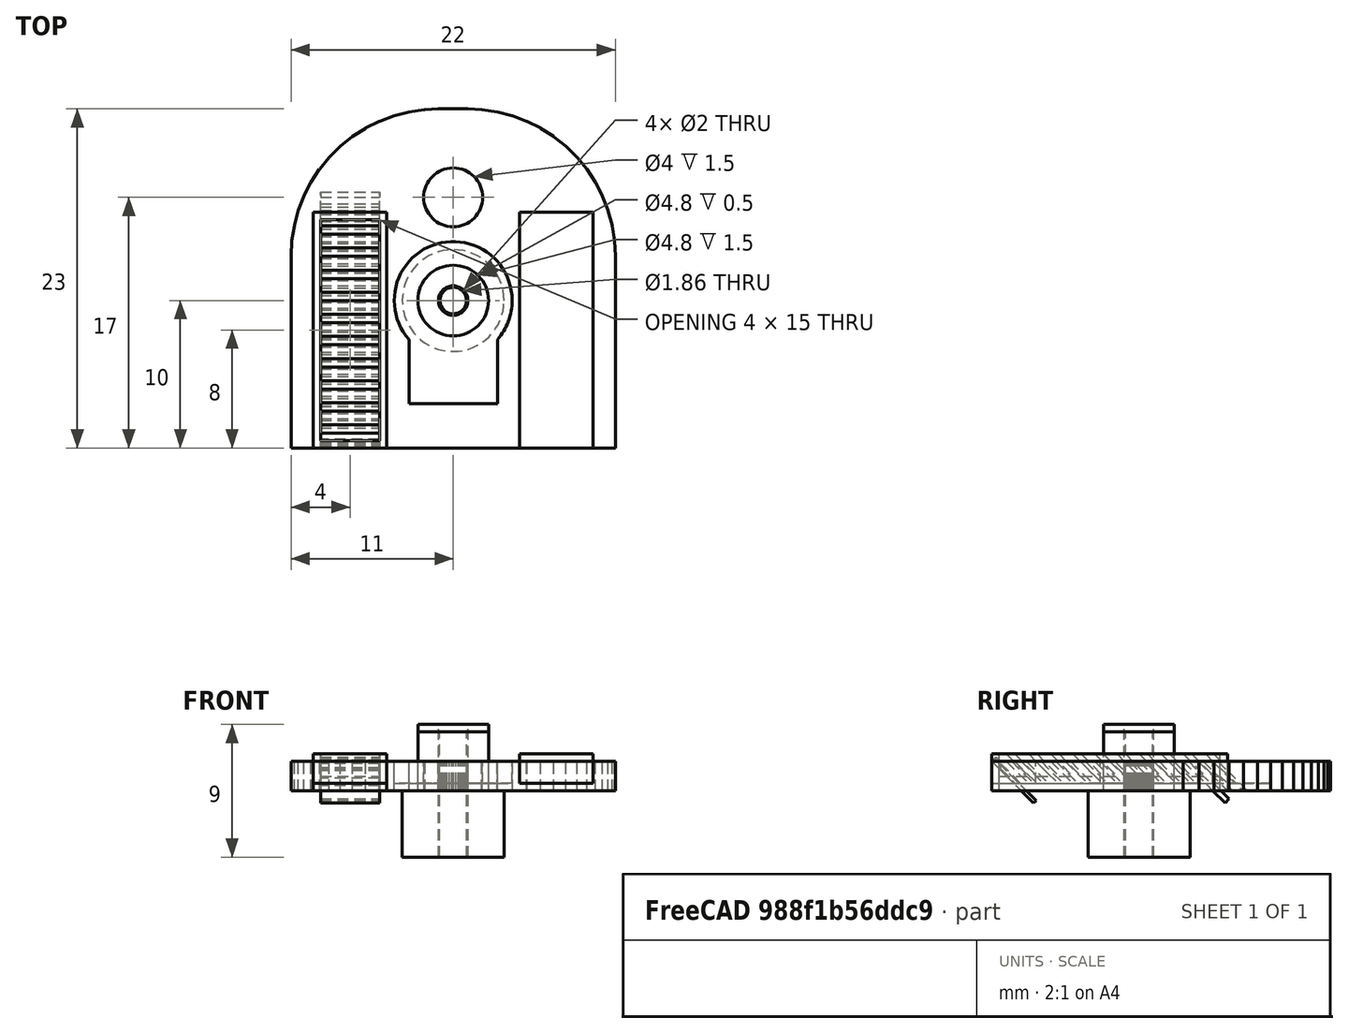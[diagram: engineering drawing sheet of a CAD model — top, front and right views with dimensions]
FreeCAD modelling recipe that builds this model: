
FCSTD DOCUMENT  (FreeCAD 0.18.3R)
Label: Engine Cowling
License: All rights reserved
LicenseURL: http://en.wikipedia.org/wiki/All_rights_reserved
objects: Part::Feature×39, Part::FeaturePython×34, Part::Box×11, Part::Cylinder×8, App::DocumentObjectGroup×8, Part::Cut×6, Part::MultiFuse×2, Mesh::Feature×1, Part::Extrusion×1
note: 101 computed .brp shape members not serialized (recipe doc carries the construction recipe); baked Part::Feature solids carry a one-line shape summary decoded from their .brp

FEATURE [Part::Cylinder] Cylinder003010  label="Cowling Insert Round002"
  Angle = 360
  AttacherType = Attacher::AttachEngine3D
  Height = 1.5
  Placement = pos=(11,17,0.5) rot=(0,0,1;0rad)
  Radius = 2
FEATURE [Part::Box] Box001005010013  label="Cube051"
  AttacherType = Attacher::AttachEngine3D
  Height = 1.5
  Length = 6
  Placement = pos=(8,3,0.5) rot=(0,0,1;0rad)
  Width = 7
FEATURE [Part::Cylinder] Cylinder003011  label="Cylinder012"
  Angle = 360
  AttacherType = Attacher::AttachEngine3D
  Height = 1.5
  Placement = pos=(11,10,0.5) rot=(0,0,1;0rad)
  Radius = 4
FEATURE [Part::MultiFuse] Fusion  label="Cowling Insert Keyhole Old"
  Shapes = -> [Box001005010013,Cylinder003011]
FEATURE [Mesh::Feature] Engine_Cowling  label="Engine Cowling"
FEATURE [Part::Feature] Engine_Cowling001
  Placement = pos=(0,0,-0.51311) rot=(0,0,1;0rad)
  shape: bbox 22 x 23 x 2.5 mm, 1292 faces, 0 solids (baked)
FEATURE [Part::Cylinder] Cylinder003006  label="Cylinder007"
  Angle = 360
  AttacherType = Attacher::AttachEngine3D
  Height = 20
  Placement = pos=(11,10,-8) rot=(0,0,1;0rad)
  Radius = 1
FEATURE [Part::Cylinder] Cylinder003005  label="Cylinder006"
  Angle = 360
  AttacherType = Attacher::AttachEngine3D
  Height = 4.5
  Placement = pos=(11,10,-5) rot=(0,0,1;0rad)
  Radius = 3.45
FEATURE [Part::Cut] Cut002002002012
  Base = -> Cylinder003005
  Tool = -> Cylinder003006
FEATURE [Part::Cylinder] Cylinder003003  label="Cylinder004"
  Angle = 360
  AttacherType = Attacher::AttachEngine3D
  Height = 4.5
  Placement = pos=(11,10,-0.5) rot=(0.707107,0,0.707107;0rad)
  Radius = 2.4
FEATURE [Part::Cut] Cut002002002013
  Base = -> Cylinder003003
  Tool = -> Cylinder003006
FEATURE [Part::FeaturePython] Connect006  label="Propeller Hub Old"  # WARN: FeaturePython — macro-defined, semantics opaque (R4)
  Objects = -> [Cut002002002012,Cut002002002013]
  Placement = pos=(0,0,0.5) rot=(0,0,1;0rad)
  Tolerance = 0
FEATURE [Part::Feature] Engine_Cowling001_cs
  Placement = pos=(0,0,-0.01) rot=(0,0,1;0rad)
  shape: bbox 22 x 23 x 3e-07 mm, 0 faces, 0 solids (baked)
FEATURE [Part::Extrusion] Extrude
  Base = -> Engine_Cowling001_cs
  Dir = (0,0,1)
  DirMode = 0
  FaceMakerClass = Part::FaceMakerBullseye
  LengthFwd = 2
  LengthRev = 0
  Solid = true
  Symmetric = false
FEATURE [Part::Box] Box  label="Cube"
  AttacherType = Attacher::AttachEngine3D
  Height = 2
  Length = 5
  Placement = pos=(1.5,0,0) rot=(0,0,1;0rad)
  Width = 16
FEATURE [Part::Box] Box001005010014  label="Cube052"
  AttacherType = Attacher::AttachEngine3D
  Height = 2
  Length = 4
  Placement = pos=(2,0.5,0.5) rot=(0,0,1;0rad)
  Width = 15
FEATURE [Part::Box] Box001005010015  label="Cube053"
  AttacherType = Attacher::AttachEngine3D
  Height = 0.25
  Length = 4
  Placement = pos=(2,0,2) rot=(-1,0,0;0.785398rad)
  Width = 4
FEATURE [Part::Cut] Cut
  Base = -> Box
  Tool = -> Box001005010014
FEATURE [Part::Feature] Face004
  Placement = pos=(1.5,0,0) rot=(0,0,1;0rad)
  shape: bbox 5 x 16 x 2e-07 mm, 1 faces, 0 solids (baked)
FEATURE [Part::Feature] Face005
  Placement = pos=(1.5,0,0) rot=(0,0,1;0rad)
  shape: bbox 5 x 16 x 2e-07 mm, 1 faces, 0 solids (baked)
FEATURE [Part::FeaturePython] Slice  # WARN: FeaturePython — macro-defined, semantics opaque (R4)
  Base = -> Box001005010015
  Mode = 1
  Tolerance = 0
  Tools = -> [Face004,Face005]
FEATURE [Part::FeaturePython] Slice_child0  label="Slice.0"  # WARN: FeaturePython — macro-defined, semantics opaque (R4)
  Base = -> Slice
  FilterType = 1
  Invert = false
  OverrideMaxVal = 0
  WindowFrom = 80
  WindowTo = 100
  items = 0
FEATURE [Part::FeaturePython] Slice_child1  label="Slice.1"  # WARN: FeaturePython — macro-defined, semantics opaque (R4)
  Base = -> Slice
  FilterType = 1
  Invert = false
  OverrideMaxVal = 0
  WindowFrom = 80
  WindowTo = 100
  items = 1
FEATURE [Part::FeaturePython] Slice_child2  label="Slice.2"  # WARN: FeaturePython — macro-defined, semantics opaque (R4)
  Base = -> Slice
  FilterType = 1
  Invert = false
  OverrideMaxVal = 0
  WindowFrom = 80
  WindowTo = 100
  items = 2
FEATURE [App::DocumentObjectGroup] GrExplode_Slice  label="Exploded Slice"
  Group = -> [Slice_child0,Slice_child1,Slice_child2]
FEATURE [Part::Feature] Slice_child0001  label="Slice.003"
  shape: bbox 4 x 2.354 x 2 mm, 6 faces (baked)
FEATURE [Part::Feature] Slice_child0002  label="Slice.004"
  Placement = pos=(0,1,0) rot=(0,0,1;0rad)
  shape: bbox 4 x 2.354 x 2 mm, 6 faces (baked)
FEATURE [Part::Feature] Slice_child0015  label="Slice.017"
  Placement = pos=(0,14,0) rot=(0,0,1;0rad)
  shape: bbox 4 x 2.354 x 2 mm, 6 faces (baked)
FEATURE [Part::Feature] Slice_child0016  label="Slice.018"
  Placement = pos=(0,15,0) rot=(0,0,1;0rad)
  shape: bbox 4 x 2.354 x 2 mm, 6 faces (baked)
FEATURE [Part::Box] Box001005010016  label="Cube054"
  AttacherType = Attacher::AttachEngine3D
  Height = 2
  Length = 5
  Placement = pos=(1.5,0,0) rot=(0,0,1;0rad)
  Width = 16
FEATURE [Part::FeaturePython] Slice001  # WARN: FeaturePython — macro-defined, semantics opaque (R4)
  Base = -> Slice_child0016
  Mode = 1
  Tolerance = 0
  Tools = -> [Box001005010016]
FEATURE [Part::FeaturePython] Slice001_child0  label="Slice001.0"  # WARN: FeaturePython — macro-defined, semantics opaque (R4)
  Base = -> Slice001
  FilterType = 1
  Invert = false
  OverrideMaxVal = 0
  WindowFrom = 80
  WindowTo = 100
  items = 0
FEATURE [Part::FeaturePython] Slice001_child1  label="Slice001.1"  # WARN: FeaturePython — macro-defined, semantics opaque (R4)
  Base = -> Slice001
  FilterType = 1
  Invert = false
  OverrideMaxVal = 0
  WindowFrom = 80
  WindowTo = 100
  items = 1
FEATURE [App::DocumentObjectGroup] GrExplode_Slice001  label="Exploded Slice001"
  Group = -> [Slice001_child0,Slice001_child1]
FEATURE [Part::Feature] Face008
  Placement = pos=(1.5,0,0) rot=(0,0,1;0rad)
  shape: bbox 5 x 2e-07 x 2 mm, 1 faces, 0 solids (baked)
FEATURE [Part::FeaturePython] Slice002  # WARN: FeaturePython — macro-defined, semantics opaque (R4)
  Base = -> Slice_child0015
  Mode = 1
  Tolerance = 0
  Tools = -> [Face008]
FEATURE [Part::FeaturePython] Slice002_child0  label="Slice002.0"  # WARN: FeaturePython — macro-defined, semantics opaque (R4)
  Base = -> Slice002
  FilterType = 1
  Invert = false
  OverrideMaxVal = 0
  WindowFrom = 80
  WindowTo = 100
  items = 0
FEATURE [Part::FeaturePython] Slice002_child1  label="Slice002.1"  # WARN: FeaturePython — macro-defined, semantics opaque (R4)
  Base = -> Slice002
  FilterType = 1
  Invert = false
  OverrideMaxVal = 0
  WindowFrom = 80
  WindowTo = 100
  items = 1
FEATURE [App::DocumentObjectGroup] GrExplode_Slice002  label="Exploded Slice002"
  Group = -> [Slice002_child0,Slice002_child1]
FEATURE [Part::Feature] Cut002002002014
  shape: bbox 5 x 16 x 2 mm, 11 faces (baked)
FEATURE [Part::Cut] Cut002002002015
  Base = -> Slice_child0001
  Tool = -> Cut002002002014
FEATURE [Part::Feature] Slice_child0017  label="Slice.019"
  shape: bbox 4 x 2.354 x 2 mm, 6 faces (baked)
FEATURE [Part::Feature] Cut002002002016
  shape: bbox 5 x 16 x 2 mm, 11 faces (baked)
FEATURE [Part::Cut] Cut002002002017
  Base = -> Slice_child0017
  Placement = pos=(0,0.1,0) rot=(0,0,1;0rad)
  Tool = -> Cut002002002016
FEATURE [Part::Feature] Slice_child0006  label="Slice.008"
  Placement = pos=(0,5,0) rot=(0,0,1;0rad)
  shape: bbox 4 x 2.354 x 2 mm, 6 faces (baked)
FEATURE [Part::Feature] Slice_child0004  label="Slice.006"
  Placement = pos=(0,3,0) rot=(0,0,1;0rad)
  shape: bbox 4 x 2.354 x 2 mm, 6 faces (baked)
FEATURE [Part::Feature] Slice_child0005  label="Slice.007"
  Placement = pos=(0,4,0) rot=(0,0,1;0rad)
  shape: bbox 4 x 2.354 x 2 mm, 6 faces (baked)
FEATURE [Part::Feature] Slice001_child0001  label="Slice001.002"
  shape: bbox 4 x 1 x 1 mm, 6 faces (baked)
FEATURE [Part::Feature] Slice002_child0001  label="Slice002.002"
  shape: bbox 4 x 2 x 2 mm, 6 faces (baked)
FEATURE [Part::Feature] Slice_child0011  label="Slice.013"
  Placement = pos=(0,10,0) rot=(0,0,1;0rad)
  shape: bbox 4 x 2.354 x 2 mm, 6 faces (baked)
FEATURE [Part::Feature] Slice_child0003  label="Slice.005"
  Placement = pos=(0,2,0) rot=(0,0,1;0rad)
  shape: bbox 4 x 2.354 x 2 mm, 6 faces (baked)
FEATURE [Part::Feature] Slice_child0007  label="Slice.009"
  Placement = pos=(0,6,0) rot=(0,0,1;0rad)
  shape: bbox 4 x 2.354 x 2 mm, 6 faces (baked)
FEATURE [Part::Feature] Slice_child0008  label="Slice.010"
  Placement = pos=(0,7,0) rot=(0,0,1;0rad)
  shape: bbox 4 x 2.354 x 2 mm, 6 faces (baked)
FEATURE [Part::Feature] Slice_child0009  label="Slice.011"
  Placement = pos=(0,8,0) rot=(0,0,1;0rad)
  shape: bbox 4 x 2.354 x 2 mm, 6 faces (baked)
FEATURE [Part::Feature] Slice_child0010  label="Slice.012"
  Placement = pos=(0,9,0) rot=(0,0,1;0rad)
  shape: bbox 4 x 2.354 x 2 mm, 6 faces (baked)
FEATURE [Part::Feature] Slice_child0012  label="Slice.014"
  Placement = pos=(0,11,0) rot=(0,0,1;0rad)
  shape: bbox 4 x 2.354 x 2 mm, 6 faces (baked)
FEATURE [Part::Feature] Slice_child0013  label="Slice.015"
  Placement = pos=(0,12,0) rot=(0,0,1;0rad)
  shape: bbox 4 x 2.354 x 2 mm, 6 faces (baked)
FEATURE [Part::Feature] Slice_child0014  label="Slice.016"
  Placement = pos=(0,13,0) rot=(0,0,1;0rad)
  shape: bbox 4 x 2.354 x 2 mm, 6 faces (baked)
FEATURE [Part::FeaturePython] Connect  # WARN: FeaturePython — macro-defined, semantics opaque (R4)
  Objects = -> [Slice_child0011,Slice_child0012,Slice_child0007,Slice_child0014,Slice_child0003,Slice_child0009,Slice_child0010,Slice_child0008,Slice_child0013,Slice_child0002,Slice_child0006,Slice_child0005,Slice001_child0001,Slice002_child0001,Slice_child0004,Cut]
  Tolerance = 0
FEATURE [Part::Feature] Cut_solid  label="Cut (Solid)"
  shape: bbox 5 x 16 x 2 mm, 11 faces (baked)
FEATURE [Part::Box] Box001005010022  label="Cube060"
  AttacherType = Attacher::AttachEngine3D
  Height = 2
  Length = 5
  Placement = pos=(1.5,0,0) rot=(0,0,1;0rad)
  Width = 16
FEATURE [Part::Feature] Slice004_child0001  label="Slice004.002"
  Placement = pos=(0,1,0) rot=(0,0,1;0rad)
  shape: bbox 4 x 2.066 x 1.5 mm, 6 faces (baked)
FEATURE [Part::Feature] Slice004_child0002  label="Slice004.003"
  Placement = pos=(0,2.5,0) rot=(0,0,1;0rad)
  shape: bbox 4 x 2.066 x 1.5 mm, 6 faces (baked)
FEATURE [Part::Feature] Slice004_child0003  label="Slice004.004"
  Placement = pos=(0,4,0) rot=(0,0,1;0rad)
  shape: bbox 4 x 2.066 x 1.5 mm, 6 faces (baked)
FEATURE [Part::Feature] Slice004_child0004  label="Slice004.005"
  Placement = pos=(0,5.5,0) rot=(0,0,1;0rad)
  shape: bbox 4 x 2.066 x 1.5 mm, 6 faces (baked)
FEATURE [Part::Feature] Slice004_child0005  label="Slice004.006"
  Placement = pos=(0,7,0) rot=(0,0,1;0rad)
  shape: bbox 4 x 2.066 x 1.5 mm, 6 faces (baked)
FEATURE [Part::Feature] Slice004_child0006  label="Slice004.007"
  Placement = pos=(0,8.5,0) rot=(0,0,1;0rad)
  shape: bbox 4 x 2.066 x 1.5 mm, 6 faces (baked)
FEATURE [Part::Feature] Slice004_child0007  label="Slice004.008"
  Placement = pos=(0,10,0) rot=(0,0,1;0rad)
  shape: bbox 4 x 2.066 x 1.5 mm, 6 faces (baked)
FEATURE [Part::Feature] Slice004_child0008  label="Slice004.009"
  Placement = pos=(0,11.5,0) rot=(0,0,1;0rad)
  shape: bbox 4 x 2.066 x 1.5 mm, 6 faces (baked)
FEATURE [Part::Feature] Slice004_child0009  label="Slice004.010"
  Placement = pos=(0,13,0) rot=(0,0,1;0rad)
  shape: bbox 4 x 2.066 x 1.5 mm, 6 faces (baked)
FEATURE [Part::Feature] Slice004_child0010  label="Slice004.011"
  Placement = pos=(0,14.5,0) rot=(0,0,1;0rad)
  shape: bbox 4 x 2.066 x 1.5 mm, 6 faces (baked)
FEATURE [Part::Feature] Slice004_child0011  label="Slice004.012"
  Placement = pos=(0,1,0) rot=(0,0,1;0rad)
  shape: bbox 4 x 2.066 x 1.5 mm, 6 faces (baked)
FEATURE [Part::Box] Box001005010023  label="Cube061"
  AttacherType = Attacher::AttachEngine3D
  Height = 2
  Length = 4
  Placement = pos=(2,0.5,0) rot=(0,0,1;0rad)
  Width = 15
FEATURE [Part::FeaturePython] Slice005  # WARN: FeaturePython — macro-defined, semantics opaque (R4)
  Base = -> Slice004_child0010
  Mode = 1
  Tolerance = 0
  Tools = -> [Box001005010023]
FEATURE [Part::FeaturePython] Slice005_child0  label="Slice005.0"  # WARN: FeaturePython — macro-defined, semantics opaque (R4)
  Base = -> Slice005
  FilterType = 1
  Invert = false
  OverrideMaxVal = 0
  WindowFrom = 80
  WindowTo = 100
  items = 0
FEATURE [Part::FeaturePython] Slice005_child1  label="Slice005.1"  # WARN: FeaturePython — macro-defined, semantics opaque (R4)
  Base = -> Slice005
  FilterType = 1
  Invert = false
  OverrideMaxVal = 0
  WindowFrom = 80
  WindowTo = 100
  items = 1
FEATURE [App::DocumentObjectGroup] GrExplode_Slice005  label="Exploded Slice005"
  Group = -> [Slice005_child0,Slice005_child1]
FEATURE [Part::Box] Box001005010017  label="Cube055"
  AttacherType = Attacher::AttachEngine3D
  Height = 0.4
  Length = 4
  Placement = pos=(2,13,2) rot=(-1,0,0;0.785398rad)
  Width = 4
FEATURE [Part::Box] Box001005010021  label="Cube059"
  AttacherType = Attacher::AttachEngine3D
  Height = 2
  Length = 4
  Placement = pos=(2,0.5,0.5) rot=(0,0,1;0rad)
  Width = 15
FEATURE [Part::FeaturePython] Slice003  # WARN: FeaturePython — macro-defined, semantics opaque (R4)
  Base = -> Box001005010017
  Mode = 1
  Tolerance = 0
  Tools = -> [Box001005010021]
FEATURE [Part::FeaturePython] Slice003_child1  label="Slice003.1"  # WARN: FeaturePython — macro-defined, semantics opaque (R4)
  Base = -> Slice003
  FilterType = 1
  Invert = false
  OverrideMaxVal = 0
  WindowFrom = 80
  WindowTo = 100
  items = 1
FEATURE [Part::FeaturePython] Slice003_child0  label="Slice003.0"  # WARN: FeaturePython — macro-defined, semantics opaque (R4)
  Base = -> Slice003
  FilterType = 1
  Invert = false
  OverrideMaxVal = 0
  Placement = pos=(0,-13,0) rot=(0,0,1;0rad)
  WindowFrom = 80
  WindowTo = 100
  items = 0
FEATURE [App::DocumentObjectGroup] GrExplode_Slice003  label="Exploded Slice003"
  Group = -> [Slice003_child0,Slice003_child1]
FEATURE [Part::FeaturePython] Slice004  # WARN: FeaturePython — macro-defined, semantics opaque (R4)
  Base = -> Slice003_child0
  Mode = 1
  Tolerance = 0
  Tools = -> [Box001005010022]
FEATURE [Part::FeaturePython] Slice004_child0  label="Slice004.0"  # WARN: FeaturePython — macro-defined, semantics opaque (R4)
  Base = -> Slice004
  FilterType = 1
  Invert = false
  OverrideMaxVal = 0
  Placement = pos=(0,1,0) rot=(0,0,1;0rad)
  WindowFrom = 80
  WindowTo = 100
  items = 0
FEATURE [Part::FeaturePython] Slice004_child1  label="Slice004.1"  # WARN: FeaturePython — macro-defined, semantics opaque (R4)
  Base = -> Slice004
  FilterType = 1
  Invert = false
  OverrideMaxVal = 0
  WindowFrom = 80
  WindowTo = 100
  items = 1
FEATURE [App::DocumentObjectGroup] GrExplode_Slice004  label="Exploded Slice004"
  Group = -> [Slice004_child0,Slice004_child1]
FEATURE [Part::FeaturePython] Connect007  label="Grate"  # WARN: FeaturePython — macro-defined, semantics opaque (R4)
  Objects = -> [Slice004_child0011,Slice004_child0006,Cut_solid,Slice004_child0001,Slice004_child0004,Slice004_child0003,Slice004_child0002,Slice004_child0008,Slice004_child0005,Slice004_child0007,Slice004_child0009,Slice005_child0]
  Placement = pos=(0,0,0.5) rot=(0,0,1;0rad)
  Tolerance = 0
FEATURE [Part::Feature] Connect006001  label="Propeller Hub001"
  Placement = pos=(0,0,0.5) rot=(0,0,1;0rad)
  shape: bbox 6.9 x 6.9 x 9 mm, 7 faces (baked)
FEATURE [Part::FeaturePython] Slice006  # WARN: FeaturePython — macro-defined, semantics opaque (R4)
  Base = -> Extrude
  Mode = 1
  Tolerance = 0
  Tools = -> [Fusion,Connect006001]
FEATURE [Part::FeaturePython] Slice006_child0  label="Slice006.0"  # WARN: FeaturePython — macro-defined, semantics opaque (R4)
  Base = -> Slice006
  FilterType = 1
  Invert = false
  OverrideMaxVal = 0
  WindowFrom = 80
  WindowTo = 100
  items = 0
FEATURE [Part::FeaturePython] Slice006_child1  label="Cowling Insert keyhole"  # WARN: FeaturePython — macro-defined, semantics opaque (R4)
  Base = -> Slice006
  FilterType = 1
  Invert = false
  OverrideMaxVal = 0
  WindowFrom = 80
  WindowTo = 100
  items = 1
FEATURE [Part::FeaturePython] Slice006_child2  label="Slice006.2"  # WARN: FeaturePython — macro-defined, semantics opaque (R4)
  Base = -> Slice006
  FilterType = 1
  Invert = false
  OverrideMaxVal = 0
  WindowFrom = 80
  WindowTo = 100
  items = 2
FEATURE [Part::FeaturePython] Slice006_child3  label="Slice006.3"  # WARN: FeaturePython — macro-defined, semantics opaque (R4)
  Base = -> Slice006
  FilterType = 1
  Invert = false
  OverrideMaxVal = 0
  WindowFrom = 80
  WindowTo = 100
  items = 3
FEATURE [Part::FeaturePython] Slice006_child4  label="Slice006.4"  # WARN: FeaturePython — macro-defined, semantics opaque (R4)
  Base = -> Slice006
  FilterType = 1
  Invert = false
  OverrideMaxVal = 0
  WindowFrom = 80
  WindowTo = 100
  items = 4
FEATURE [Part::FeaturePython] Slice006_child5  label="Slice006.5"  # WARN: FeaturePython — macro-defined, semantics opaque (R4)
  Base = -> Slice006
  FilterType = 1
  Invert = false
  OverrideMaxVal = 0
  WindowFrom = 80
  WindowTo = 100
  items = 5
FEATURE [App::DocumentObjectGroup] GrExplode_Slice006  label="Exploded Slice006"
  Group = -> [Slice006_child0,Slice006_child1,Slice006_child2,Slice006_child3,Slice006_child4,Slice006_child5]
FEATURE [Part::Box] Box001005010024  label="Cube062"
  AttacherType = Attacher::AttachEngine3D
  Height = 2
  Length = 5
  Placement = pos=(1.5,0,0.5) rot=(0,0,1;0rad)
  Width = 16
FEATURE [Part::Box] Box001005010025  label="Cube063"
  AttacherType = Attacher::AttachEngine3D
  Height = 2
  Length = 5
  Placement = pos=(15.5,0,0.5) rot=(0,0,1;0rad)
  Width = 16
FEATURE [Part::FeaturePython] Slice007  # WARN: FeaturePython — macro-defined, semantics opaque (R4)
  Base = -> Slice006_child0
  Mode = 1
  Tolerance = 0
  Tools = -> [Cylinder003010,Box001005010024,Box001005010025,Slice006_child1]
FEATURE [Part::FeaturePython] Slice007_child0  label="Cowling"  # WARN: FeaturePython — macro-defined, semantics opaque (R4)
  Base = -> Slice007
  FilterType = 1
  Invert = false
  OverrideMaxVal = 0
  WindowFrom = 80
  WindowTo = 100
  items = 0
FEATURE [Part::FeaturePython] Slice007_child1  label="Slice007.1"  # WARN: FeaturePython — macro-defined, semantics opaque (R4)
  Base = -> Slice007
  FilterType = 1
  Invert = false
  OverrideMaxVal = 0
  WindowFrom = 80
  WindowTo = 100
  items = 1
FEATURE [Part::FeaturePython] Slice007_child2  label="Slice007.2"  # WARN: FeaturePython — macro-defined, semantics opaque (R4)
  Base = -> Slice007
  FilterType = 1
  Invert = false
  OverrideMaxVal = 0
  WindowFrom = 80
  WindowTo = 100
  items = 2
FEATURE [Part::FeaturePython] Slice007_child3  label="Cowling Insert Round"  # WARN: FeaturePython — macro-defined, semantics opaque (R4)
  Base = -> Slice007
  FilterType = 1
  Invert = false
  OverrideMaxVal = 0
  WindowFrom = 80
  WindowTo = 100
  items = 3
FEATURE [App::DocumentObjectGroup] GrExplode_Slice007  label="Exploded Slice007"
  Group = -> [Slice007_child0,Slice007_child1,Slice007_child2,Slice007_child3]
FEATURE [Part::Cylinder] Cylinder003012  label="Cylinder013"
  Angle = 360
  AttacherType = Attacher::AttachEngine3D
  Height = 20
  Placement = pos=(11,10,-8) rot=(0,0,1;0rad)
  Radius = 0.93
FEATURE [Part::Cylinder] Cylinder003013  label="Cylinder014"
  Angle = 360
  AttacherType = Attacher::AttachEngine3D
  Height = 4.5
  Placement = pos=(11,10,-0.5) rot=(0.707107,0,0.707107;0rad)
  Radius = 2.4
FEATURE [Part::Cylinder] Cylinder003014  label="Cylinder015"
  Angle = 360
  AttacherType = Attacher::AttachEngine3D
  Height = 4.5
  Placement = pos=(11,10,-4.5) rot=(0,0,1;0rad)
  Radius = 3.45
FEATURE [Part::MultiFuse] Fusion001
  Shapes = -> [Cylinder003014,Cylinder003013]
FEATURE [Part::Cut] Cut002002002018  label="Propeller Hub"
  Base = -> Fusion001
  Tool = -> Cylinder003012
